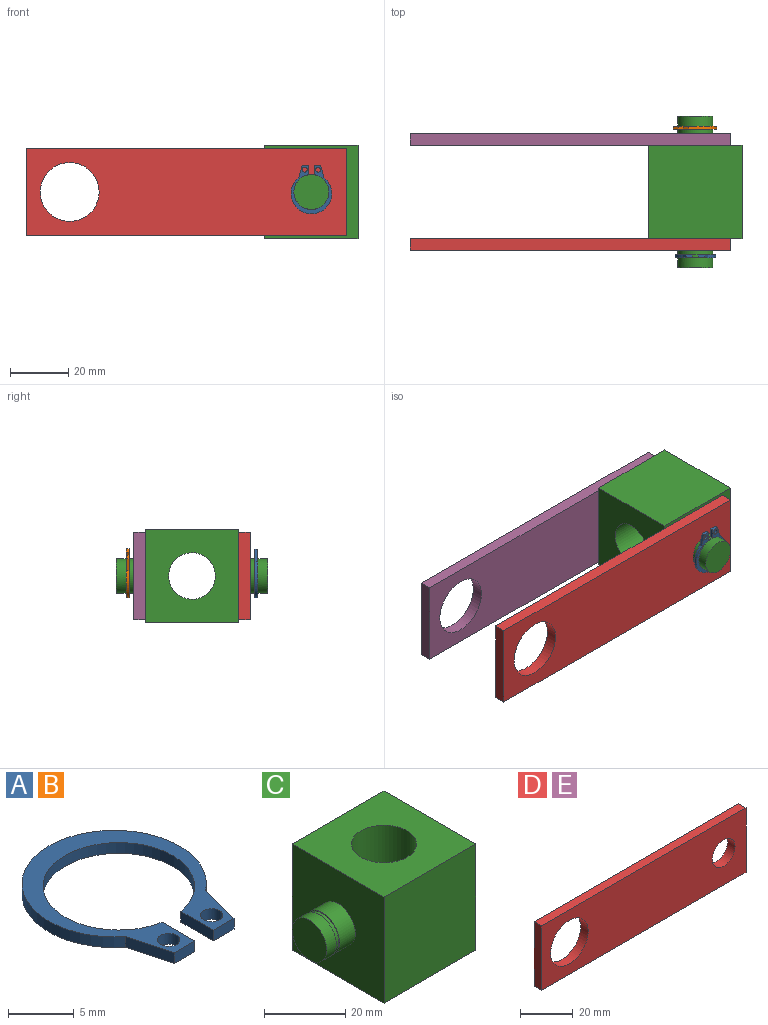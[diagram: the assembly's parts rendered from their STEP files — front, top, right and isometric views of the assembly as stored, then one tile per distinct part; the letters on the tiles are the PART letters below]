
ASSEMBLY  parts=5 mates=4
PART A: 12 faces, bbox 14x16.7x1 mm
  f0: plane 3.5x1mm, normal (1,0,0), area 3.5mm2, adj f1,f8,f10,f11
  f1: cylinder r=5.75mm len=11.5mm, axis (0,0,-1), area 34.1mm2, adj f0,f2,f10,f11
  f2: plane 3.5x1mm, normal (-1,0,0), area 3.5mm2, adj f1,f3,f10,f11
  f3: plane 2.2x1mm, normal (0,-1,0), area 2.2mm2, adj f2,f4,f10,f11
  f4: plane 4.15x1.11mm, normal (0.97,-0.26,0), area 4.3mm2, adj f3,f5,f10,f11
  f5: cylinder r=7mm len=14mm, axis (0,0,-1), area 34.7mm2, adj f4,f6,f10,f11
  f6: plane 4.15x1.11mm, normal (-0.97,-0.26,0), area 4.3mm2, adj f5,f8,f10,f11
  f7: cylinder r=0.85mm len=1.7mm, axis (0,0,-1), area 5.3mm2, adj f10,f11
  f8: plane 2.2x1mm, normal (0,-1,0), area 2.2mm2, adj f0,f6,f10,f11
  f9: cylinder r=0.85mm len=1.7mm, axis (0,0,-1), area 5.3mm2, adj f10,f11
  f10: plane 16.66x14mm, normal (0,0,1), area 61.1mm2, adj f0,f1,f2,f3,f4,f5,f6,f7
  f11: plane 16.66x14mm, normal (0,0,-1), area 61.1mm2, adj f0,f1,f2,f3,f4,f5,f6,f7
PART B: same geometry as A
PART C: 19 faces, bbox 52x32x32 mm
  f0: cylinder r=8mm len=32mm, axis (0,0,1), area 1608.5mm2, adj f6,f7
  f1: cylinder r=6mm len=12mm, axis (-1,0,0), area 207.3mm2, adj f5,f9
  f2: plane 32x32mm, normal (0,1,0), area 1024mm2, adj f3,f5,f6,f7
  f3: plane 32x32mm, normal (-1,0,0), area 910.9mm2, adj f2,f4,f6,f7,f13
  f4: plane 32x32mm, normal (0,-1,0), area 1024mm2, adj f3,f5,f6,f7
  f5: plane 32x32mm, normal (1,0,0), area 910.9mm2, adj f1,f2,f4,f6,f7
  f6: plane 32x32mm, normal (0,0,1), area 822.9mm2, adj f0,f2,f3,f4,f5
  f7: plane 32x32mm, normal (0,0,-1), area 822.9mm2, adj f0,f2,f3,f4,f5
  f8: plane 12x12mm, normal (-1,0,0), area 9.2mm2, adj f10,f12
  f9: plane 12x12mm, normal (1,0,0), area 9.2mm2, adj f1,f10
  f10: cylinder r=5.75mm len=11.5mm, axis (-1,0,0), area 39.7mm2, adj f8,f9
  f11: plane 12x12mm, normal (1,0,0), area 113.1mm2, adj f12
  f12: cylinder r=6mm len=12mm, axis (-1,0,0), area 128.2mm2, adj f8,f11
  f13: cylinder r=6mm len=12mm, axis (1,0,0), area 207.3mm2, adj f3,f15
  f14: plane 12x12mm, normal (1,0,0), area 9.2mm2, adj f16,f18
  f15: plane 12x12mm, normal (-1,0,0), area 9.2mm2, adj f13,f16
  f16: cylinder r=5.75mm len=11.5mm, axis (1,0,0), area 39.7mm2, adj f14,f15
  f17: plane 12x12mm, normal (-1,0,0), area 113.1mm2, adj f18
  f18: cylinder r=6mm len=12mm, axis (1,0,0), area 128.2mm2, adj f14,f17
PART D: 8 faces, bbox 110x4x30 mm
  f0: plane 30x4mm, normal (-1,0,0), area 120mm2, adj f1,f4,f6,f7
  f1: plane 110x4mm, normal (0,0,-1), area 440mm2, adj f0,f2,f6,f7
  f2: plane 30x4mm, normal (1,0,0), area 120mm2, adj f1,f4,f6,f7
  f3: cylinder r=10.1mm len=20.2mm, axis (0,1,0), area 253.8mm2, adj f6,f7
  f4: plane 110x4mm, normal (0,0,1), area 440mm2, adj f0,f2,f6,f7
  f5: cylinder r=6.1mm len=12.2mm, axis (0,1,0), area 153.3mm2, adj f6,f7
  f6: plane 110x30mm, normal (0,-1,0), area 2862.6mm2, adj f0,f1,f2,f3,f4,f5
  f7: plane 110x30mm, normal (0,1,0), area 2862.6mm2, adj f0,f1,f2,f3,f4,f5
PART E: same geometry as D
PLACE A rot(axis=(-1,0,0),90deg) t=(-4.96,-55.77,35.3)mm
PLACE B rot(axis=(0.21,0.69,-0.69),156.7deg) t=(-4.96,-10.77,35.3)mm
PLACE C rot(axis=(0.58,0.58,0.58),120deg) t=(-20.96,-49.27,51.3)mm
PLACE D rot(axis=(-0.33,0.91,0.23),0deg) t=(-102.96,-49.27,20.3)mm
PLACE E t=(-102.96,-13.27,20.3)mm
MATE revolute B.f1 <-> C.f1  axis (0,-1,0) through (-4.96,-11.77,35.3)mm
MATE revolute D.f5 <-> C.f1  axis (0,1,0) through (-4.96,-49.27,35.3)mm
MATE revolute E.f5 <-> C.f1  axis (0,-1,0) through (-4.96,-17.27,35.3)mm
MATE revolute A.f1 <-> C.f1  axis (0,1,0) through (-4.96,-54.77,35.3)mm
